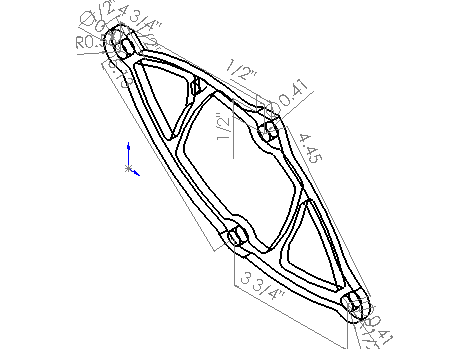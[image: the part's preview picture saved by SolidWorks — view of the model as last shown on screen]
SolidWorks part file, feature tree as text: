
SOLIDWORKS PART (.sldprt)
format: sldprt  version: not decoded by parser v0  size: 542,720 bytes
history: native  units: mm
features: sketch x305, extrude x1 + 5 further entries (+10 scaffold rows collapsed; 56 parser-record rows omitted)
feature tree (377):
  "Annotations"  RD1=95.25mm RD2=113.058536mm RD3=120.65mm RD4=130.291107mm RD6=10.3124mm RD5=12.7mm RD7=12.7mm RD8=12.7mm RD9=12.7mm RD10=12.7mm RD11=10.3124mm RD12=10.3124mm RD13=14.199032mm
  scaffold x10  (default folders/planes/origin — collapsed)
  sketch  "Sketch2"  dims[c1.D1=6.35mm c1.D2=6.35mm c1.D3=3.175mm c1.D4=3.175mm c2.D1=304.8mm c3.D1=~44.215175deg c4.D1=~862.162868mm c5.D1=~23.628086mm c6.D1=~757.905383mm c7.D1=6.35mm c7.D2=6.35mm c8.D1=3.048mm c8.D2=3.048mm c9.D1=1.524mm c9.D2=1.524mm c10.D1=6.35mm]
  extrude  "Extrude3"  Depth=6.35mm RestraintType=1
  sketch  "Value"
  sketch  "cosRestraintComp:1"
  sketch  "cosRestraintComp:2"
  sketch  "cosRestraintComp:3"
  sketch  "cosRestraintComp:4"
  sketch  "cosRestraintComp:5"
  sketch  "cosRestraintComp:6"
  sketch  "Unit"
  sketch  "AnalysisType"
  sketch  "MeshType"
  sketch  "cosRestraintCompCheck1"
  sketch  "cosRestraintCompCheck2"
  sketch  "cosRestraintCompCheck3"
  sketch  "cosRestraintCompCheck4"
  sketch  "cosRestraintCompCheck5"
  sketch  "cosRestraintCompCheck6"
  sketch  "cosRestraintRefPlaneSet"
  sketch  "cosRestraintRefPlaneOrigin1"
  sketch  "cosRestraintRefPlaneOrigin2"
  sketch  "cosRestraintRefPlaneOrigin3"
  sketch  "cosRestraintRefPlaneXDir1"
  sketch  "cosRestraintRefPlaneXDir2"
  sketch  "cosRestraintRefPlaneXDir3"
  sketch  "cosRestraintRefPlaneNormal1"
  sketch  "cosRestraintRefPlaneNormal2"
  sketch  "cosRestraintRefPlaneNormal3"
  sketch  "cosRestraintCoordSystemType"
  sketch  "cosRestraintFaceTypeMask"  dims[cosFMVItemName=0.0deg cosLBCSymbolColor=0.0deg]
  sketch  "cosLBCState"
  sketch  "RestraintType"
  sketch  "Value"
  sketch  "cosRestraintComp:1"
  sketch  "cosRestraintComp:2"
  sketch  "cosRestraintComp:3"
  sketch  "cosRestraintComp:4"
  sketch  "cosRestraintComp:5"
  sketch  "cosRestraintComp:6"
  sketch  "Unit"
  sketch  "AnalysisType"
  sketch  "MeshType"
  sketch  "cosRestraintCompCheck1"
  sketch  "cosRestraintCompCheck2"
  sketch  "cosRestraintCompCheck3"
  sketch  "cosRestraintCompCheck4"
  sketch  "cosRestraintCompCheck5"
  sketch  "cosRestraintCompCheck6"
  sketch  "cosRestraintRefPlaneSet"
  sketch  "cosRestraintRefPlaneOrigin1"
  sketch  "cosRestraintRefPlaneOrigin2"
  sketch  "cosRestraintRefPlaneOrigin3"
  sketch  "cosRestraintRefPlaneXDir1"
  sketch  "cosRestraintRefPlaneXDir2"
  sketch  "cosRestraintRefPlaneXDir3"
  sketch  "cosRestraintRefPlaneNormal1"
  sketch  "cosRestraintRefPlaneNormal2"
  sketch  "cosRestraintRefPlaneNormal3"  dims[cosRestraintRefPlaneName=0.0deg]
  sketch  "cosRestraintCoordSystemType"
  sketch  "cosRestraintFaceTypeMask"  dims[cosFMVItemName=0.0deg cosLBCSymbolColor=0.0deg]
  sketch  "cosLBCState"
  "freq:Restraint-2"
  sketch  "RestraintType"
  sketch  "Value"
  sketch  "cosRestraintComp:1"
  sketch  "cosRestraintComp:2"
  sketch  "cosRestraintComp:3"
  sketch  "cosRestraintComp:4"
  sketch  "cosRestraintComp:5"
  sketch  "cosRestraintComp:6"
  sketch  "Unit"
  sketch  "AnalysisType"
  sketch  "MeshType"
  sketch  "cosRestraintCompCheck1"
  sketch  "cosRestraintCompCheck2"
  sketch  "cosRestraintCompCheck3"
  sketch  "cosRestraintCompCheck4"
  sketch  "cosRestraintCompCheck5"
  sketch  "cosRestraintCompCheck6"
  sketch  "cosRestraintRefPlaneSet"
  sketch  "cosRestraintRefPlaneOrigin1"
  sketch  "cosRestraintRefPlaneOrigin2"
  sketch  "cosRestraintRefPlaneOrigin3"
  sketch  "cosRestraintRefPlaneXDir1"
  sketch  "cosRestraintRefPlaneXDir2"
  sketch  "cosRestraintRefPlaneXDir3"
  sketch  "cosRestraintRefPlaneNormal1"
  sketch  "cosRestraintRefPlaneNormal2"
  sketch  "cosRestraintRefPlaneNormal3"  dims[cosRestraintRefPlaneName=0.0deg]
  sketch  "cosRestraintCoordSystemType"
  sketch  "cosRestraintFaceTypeMask"  dims[cosFMVItemName=0.0deg cosLBCSymbolColor=0.0deg]
  sketch  "cosLBCState"
  "freq:Force-1"
  sketch  "cosForceComp:1"
  sketch  "cosForceComp:2"
  sketch  "cosForceComp:3"
  sketch  "cosForceComp:4"
  sketch  "cosForceComp:5"
  sketch  "cosForceComp:6"
  sketch  "cosForceTorqueNF"
  sketch  "cosForceCompCheck1"
  sketch  "cosForceCompCheck2"
  sketch  "cosForceCompCheck3"
  sketch  "cosForceCompCheck4"
  sketch  "cosForceCompCheck5"
  sketch  "cosForceCompCheck6"
  sketch  "Unit"
  sketch  "AnalysisType"
  sketch  "MeshType"
  sketch  "cosForceRefPlaneSet"
  sketch  "cosForceRefPlaneOrigin1"
  sketch  "cosForceRefPlaneOrigin2"
  sketch  "cosForceRefPlaneOrigin3"
  sketch  "cosForceRefPlaneXDir1"
  sketch  "cosForceRefPlaneXDir2"
  sketch  "cosForceRefPlaneXDir3"
  sketch  "cosForceRefPlaneNormal1"
  sketch  "cosForceRefPlaneNormal2"
  sketch  "cosForceRefPlaneNormal3"  dims[cosForceRefPlaneName=0.0deg]
  sketch  "cosForceCoordSystemType"
  sketch  "cosForceType"  dims[cosFMVItemName=0.0deg]
  sketch  "cosDistributionType"  dims[cosDistributionCoordSysName=0.0deg]
  sketch  "cosDistributionCoef1"
  sketch  "cosDistributionCoef2"
  sketch  "cosDistributionCoef3"
  sketch  "cosDistributionCoef4"
  sketch  "cosDistributionCoef5"
  sketch  "cosDistributionCoef6"  dims[cosLBCSymbolColor=0.0deg]
  sketch  "cosLBCState"  dims[cosForce7=0.0]
  sketch  "cosForceComp:1"
  sketch  "cosForceComp:2"
  sketch  "cosForceComp:3"
  sketch  "cosForceComp:4"
  sketch  "cosForceComp:5"
  sketch  "cosForceComp:6"
  sketch  "cosForceTorqueNF"
  sketch  "cosForceCompCheck1"
  sketch  "cosForceCompCheck2"
  sketch  "cosForceCompCheck3"
  sketch  "cosForceCompCheck4"
  sketch  "cosForceCompCheck5"
  sketch  "cosForceCompCheck6"
  sketch  "Unit"
  sketch  "AnalysisType"
  sketch  "MeshType"
  sketch  "cosForceRefPlaneSet"
  sketch  "cosForceRefPlaneOrigin1"
  sketch  "cosForceRefPlaneOrigin2"
  sketch  "cosForceRefPlaneOrigin3"
  sketch  "cosForceRefPlaneXDir1"
  sketch  "cosForceRefPlaneXDir2"
  sketch  "cosForceRefPlaneXDir3"
  sketch  "cosForceRefPlaneNormal1"
  sketch  "cosForceRefPlaneNormal2"
  sketch  "cosForceRefPlaneNormal3"  dims[cosForceRefPlaneName=0.0deg]
  sketch  "cosForceCoordSystemType"
  sketch  "cosForceType"  dims[cosFMVItemName=0.0deg]
  sketch  "cosDistributionType"  dims[cosDistributionCoordSysName=0.0deg]
  sketch  "cosDistributionCoef1"
  sketch  "cosDistributionCoef2"
  sketch  "cosDistributionCoef3"
  sketch  "cosDistributionCoef4"
  sketch  "cosDistributionCoef5"
  sketch  "cosDistributionCoef6"  dims[cosLBCSymbolColor=0.0deg]
  sketch  "cosLBCState"
  "freq:Force-2"
  sketch  "cosForceComp:1"
  sketch  "cosForceComp:2"
  sketch  "cosForceComp:3"
  sketch  "cosForceComp:4"
  sketch  "cosForceComp:5"
  sketch  "cosForceComp:6"
  sketch  "cosForceTorqueNF"
  sketch  "cosForceCompCheck1"
  sketch  "cosForceCompCheck2"
  sketch  "cosForceCompCheck3"
  sketch  "cosForceCompCheck4"
  sketch  "cosForceCompCheck5"
  sketch  "cosForceCompCheck6"
  sketch  "Unit"
  sketch  "AnalysisType"
  sketch  "MeshType"
  sketch  "cosForceRefPlaneSet"
  sketch  "cosForceRefPlaneOrigin1"
  sketch  "cosForceRefPlaneOrigin2"
  sketch  "cosForceRefPlaneOrigin3"
  sketch  "cosForceRefPlaneXDir1"
  sketch  "cosForceRefPlaneXDir2"
  sketch  "cosForceRefPlaneXDir3"
  sketch  "cosForceRefPlaneNormal1"
  sketch  "cosForceRefPlaneNormal2"
  sketch  "cosForceRefPlaneNormal3"  dims[cosForceRefPlaneName=0.0deg]
  sketch  "cosForceCoordSystemType"
  sketch  "cosForceType"  dims[cosFMVItemName=0.0deg]
  sketch  "cosDistributionType"  dims[cosDistributionCoordSysName=0.0deg]
  sketch  "cosDistributionCoef1"
  sketch  "cosDistributionCoef2"
  sketch  "cosDistributionCoef3"
  sketch  "cosDistributionCoef4"
  sketch  "cosDistributionCoef5"
  sketch  "cosDistributionCoef6"  dims[cosLBCSymbolColor=0.0deg]
  sketch  "cosLBCState"
  parser-record x56  (decoder bookkeeping rows leaked as tree rows — omitted from the tree; the rows remain in map.json)
  sketch  "faceID"  dims[cosFaceID=0.0]
  sketch  "faceID"
  sketch  "faceID"
  sketch  "faceID"
  sketch  "faceID"
  sketch  "faceID"
  sketch  "faceID"
  sketch  "faceID"
  sketch  "faceID"
  sketch  "faceID"
  sketch  "faceID"
  sketch  "faceID"
  sketch  "faceID"
  sketch  "faceID"
  sketch  "faceID"
  sketch  "faceID"
  sketch  "faceID"
  sketch  "faceID"
  sketch  "faceID"
  sketch  "faceID"
  sketch  "faceID"
  sketch  "faceID"
  sketch  "faceID"
  sketch  "faceID"
  sketch  "faceID"
  sketch  "faceID"
  sketch  "faceID"
  sketch  "faceID"
  sketch  "faceID"
  sketch  "faceID"
  sketch  "faceID"
  sketch  "faceID"
  sketch  "faceID"
  sketch  "faceID"
  sketch  "faceID"
  sketch  "faceID"
  sketch  "faceID"
  sketch  "faceID"
  sketch  "faceID"
  sketch  "faceID"
  sketch  "faceID"
  sketch  "faceID"
  sketch  "faceID"
  sketch  "faceID"
  sketch  "faceID"
  sketch  "faceID"
  sketch  "faceID"
  sketch  "faceID"
  sketch  "faceID"
  sketch  "faceID"
  sketch  "faceID"
  sketch  "faceID"
  sketch  "faceID"
  sketch  "faceID"
  sketch  "faceID"
  sketch  "faceID"
  sketch  "faceID"
  "freq:Material-1"
  sketch  "cosMaterialEX"
  sketch  "cosMaterialNUXY"
  sketch  "cosMaterialGXY"
  sketch  "cosMaterialALPX"
  sketch  "cosMaterialDENS"
  sketch  "cosMaterialKX"
  sketch  "cosMaterialC"
  sketch  "Units"
  sketch  "AnalysisType"
  sketch  "MeshType"
  sketch  "cosMaterialSIGYLD"
  sketch  "cosMaterialSIGXT"
  sketch  "cosMaterialSIGXC"  dims[sMaterialSourceName=0.0deg sMaterialName=0.0deg cosFMVItemName=0.0deg cosMaterialName=0.0deg cosComponentName=0.0deg]
  sketch  "cosMaterialModel"
  sketch  "cosMaterialEY"
  sketch  "cosMaterialEZ"
  sketch  "cosMaterialNUXZ"
  sketch  "cosMaterialNUYZ"
  sketch  "cosMaterialGXZ"
  sketch  "cosMaterialGYZ"
  sketch  "cosMaterialALPY"
  sketch  "cosMaterialALPZ"
  sketch  "cosMaterialKY"
  sketch  "cosMaterialKZ"  dims[cosMaterialType=0.0deg cosMaterialLibFile=0.0deg cosMaterialRefPlaneName=0.0deg]
  sketch  "cosMaterialSource"  dims[cosMaterial7=0.0]
  sketch  "cosMaterialEX"
  sketch  "cosMaterialNUXY"
  sketch  "cosMaterialGXY"
  sketch  "cosMaterialALPX"
  sketch  "cosMaterialDENS"
  sketch  "cosMaterialKX"
  sketch  "cosMaterialC"
  sketch  "Units"
  sketch  "AnalysisType"
  sketch  "MeshType"
  sketch  "cosMaterialSIGYLD"
  sketch  "cosMaterialSIGXT"
  sketch  "cosMaterialSIGXC"  dims[sMaterialSourceName=0.0deg sMaterialName=0.0deg cosFMVItemName=0.0deg cosMaterialName=0.0deg cosComponentName=0.0deg]
  sketch  "cosMaterialModel"
  sketch  "cosMaterialEY"
  sketch  "cosMaterialEZ"
  sketch  "cosMaterialNUXZ"
  sketch  "cosMaterialNUYZ"
  sketch  "cosMaterialGXZ"
  sketch  "cosMaterialGYZ"
  sketch  "cosMaterialALPY"
  sketch  "cosMaterialALPZ"
  sketch  "cosMaterialKY"
  sketch  "cosMaterialKZ"  dims[cosMaterialType=0.0deg cosMaterialLibFile=0.0deg cosMaterialRefPlaneName=0.0deg]
  sketch  "cosMaterialSource"
decode coverage: 26 of 306 modeling features carry decoded parameters; 5 rows unclassified (native names shown)
note: ~ marks probable driven/reference dimensions
note: suppression state not decoded; provenance and decode notes live in map.json
